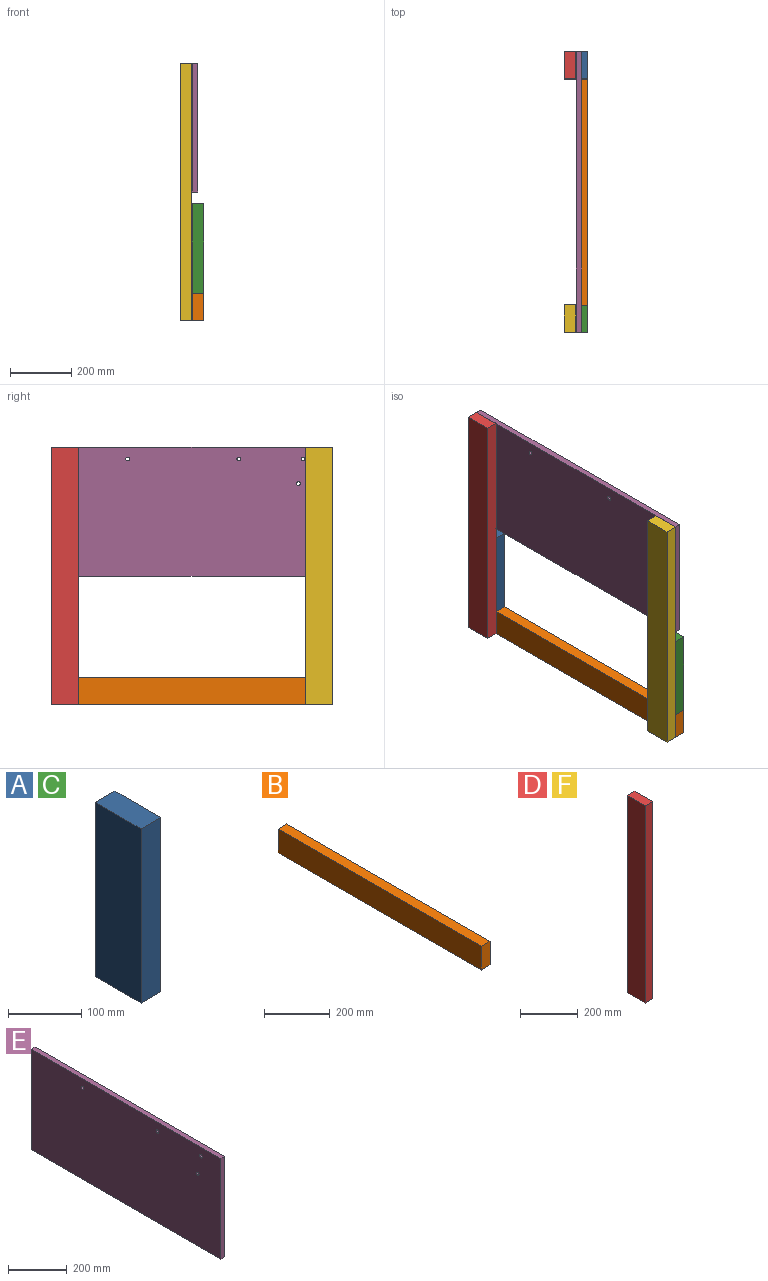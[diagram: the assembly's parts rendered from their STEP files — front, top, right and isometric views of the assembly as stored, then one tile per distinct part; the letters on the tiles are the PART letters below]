
ASSEMBLY  parts=6 mates=15
PART A: 6 faces, bbox 38.1x88.9x292.1 mm
  f0: plane 292.1x38.1mm, normal (0,1,0), area 11129mm2, adj f1,f3,f4,f5
  f1: plane 292.1x88.9mm, normal (-1,0,0), area 25967.7mm2, adj f0,f2,f4,f5
  f2: plane 292.1x38.1mm, normal (0,-1,0), area 11129mm2, adj f1,f3,f4,f5
  f3: plane 292.1x88.9mm, normal (1,0,0), area 25967.7mm2, adj f0,f2,f4,f5
  f4: plane 88.9x38.1mm, normal (0,0,1), area 3387.1mm2, adj f0,f1,f2,f3
  f5: plane 88.9x38.1mm, normal (0,0,-1), area 3387.1mm2, adj f0,f1,f2,f3
PART B: 6 faces, bbox 38.1x876.3x88.9 mm
  f0: plane 876.3x38.1mm, normal (0,0,1), area 33387mm2, adj f1,f3,f4,f5
  f1: plane 876.3x88.9mm, normal (-1,0,0), area 77903.1mm2, adj f0,f2,f4,f5
  f2: plane 876.3x38.1mm, normal (0,0,-1), area 33387mm2, adj f1,f3,f4,f5
  f3: plane 876.3x88.9mm, normal (1,0,0), area 77903.1mm2, adj f0,f2,f4,f5
  f4: plane 88.9x38.1mm, normal (0,1,0), area 3387.1mm2, adj f0,f1,f2,f3
  f5: plane 88.9x38.1mm, normal (0,-1,0), area 3387.1mm2, adj f0,f1,f2,f3
PART C: same geometry as A
PART D: 6 faces, bbox 38.1x88.9x838.2 mm
  f0: plane 838.2x88.9mm, normal (-1,0,0), area 74516mm2, adj f1,f3,f4,f5
  f1: plane 838.2x38.1mm, normal (0,-1,0), area 31935.4mm2, adj f0,f2,f4,f5
  f2: plane 838.2x88.9mm, normal (1,0,0), area 74516mm2, adj f1,f3,f4,f5
  f3: plane 838.2x38.1mm, normal (0,1,0), area 31935.4mm2, adj f0,f2,f4,f5
  f4: plane 88.9x38.1mm, normal (0,0,1), area 3387.1mm2, adj f0,f1,f2,f3
  f5: plane 88.9x38.1mm, normal (0,0,-1), area 3387.1mm2, adj f0,f1,f2,f3
PART E: 10 faces, bbox 19.1x914.4x419.1 mm
  f0: plane 914.4x19.05mm, normal (0,0,1), area 17419.3mm2, adj f1,f3,f4,f5
  f1: plane 914.4x419.1mm, normal (-1,0,0), area 382718.3mm2, adj f0,f2,f4,f5,f6,f7,f8,f9
  f2: plane 914.4x19.05mm, normal (0,0,-1), area 17419.3mm2, adj f1,f3,f4,f5
  f3: plane 914.4x419.1mm, normal (1,0,0), area 382718.3mm2, adj f0,f2,f4,f5,f6,f7,f8,f9
  f4: plane 419.1x19.05mm, normal (0,1,0), area 7983.9mm2, adj f0,f1,f2,f3
  f5: plane 419.1x19.05mm, normal (0,-1,0), area 7983.9mm2, adj f0,f1,f2,f3
  f6: cylinder r=6.35mm len=19.05mm, axis (1,0,0), area 760.1mm2, adj f1,f3
  f7: cylinder r=6.35mm len=19.05mm, axis (-1,0,0), area 760.1mm2, adj f1,f3
  f8: cylinder r=6.35mm len=19.05mm, axis (-1,0,0), area 760.1mm2, adj f1,f3
  f9: cylinder r=6.35mm len=19.05mm, axis (-1,0,0), area 760.1mm2, adj f1,f3
PART F: same geometry as D
PLACE A t=(394.49,716.98,-1362.78)mm
PLACE B t=(407.12,-197.42,-1376.69)mm
PLACE C t=(394.49,-108.52,-1362.78)mm
PLACE D t=(378.42,716.98,-1451.68)mm
PLACE E t=(410.15,-197.42,-930.16)mm
PLACE F t=(378.42,-108.52,-1451.68)mm
MATE planar C.f3 <-> A.f3  axis (1,0,0) through (369.04,-152.97,-1216.73)mm
MATE planar E.f4 <-> D.f3  axis (0,1,0) through (340.46,716.98,-823.03)mm
MATE planar F.f1 <-> C.f2  axis (0,-1,0) through (311.89,-197.42,-1032.58)mm
MATE planar F.f1 <-> B.f5  axis (0,-1,0) through (311.89,-197.42,-1032.58)mm
MATE planar F.f2 <-> B.f1  axis (1,0,0) through (330.94,-152.97,-1032.58)mm
MATE planar B.f0 <-> C.f5  axis (0,0,1) through (349.99,240.73,-1362.78)mm
MATE planar E.f0 <-> D.f4  axis (0,0,1) through (340.46,259.78,-613.48)mm
MATE planar F.f2 <-> C.f1  axis (1,0,0) through (330.94,-152.97,-1032.58)mm
MATE planar E.f0 <-> F.f4  axis (0,0,1) through (340.46,259.78,-613.48)mm
MATE planar E.f1 <-> F.f2  axis (-1,0,0) through (330.94,260,-823.23)mm
MATE planar F.f5 <-> B.f2  axis (0,0,-1) through (311.89,-152.97,-1451.68)mm
MATE planar E.f5 <-> F.f1  axis (0,-1,0) through (340.46,-197.42,-613.48)mm
MATE planar B.f0 <-> A.f5  axis (0,0,1) through (349.99,240.73,-1362.78)mm
MATE planar D.f3 <-> A.f0  axis (0,1,0) through (311.89,716.98,-1032.58)mm
MATE planar E.f1 <-> D.f2  axis (-1,0,0) through (330.94,260,-823.23)mm
